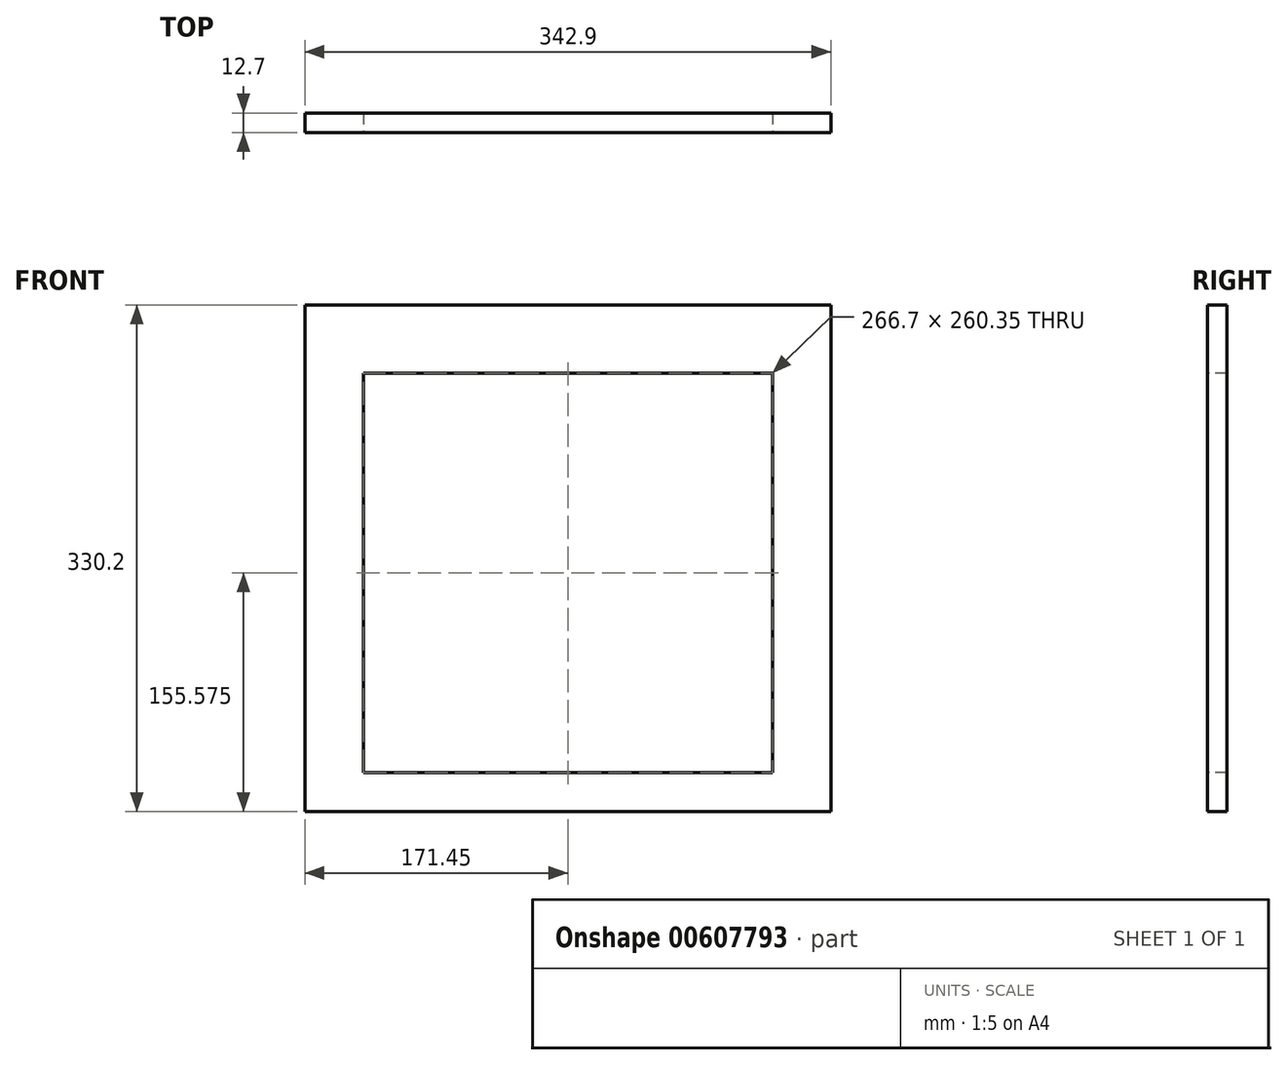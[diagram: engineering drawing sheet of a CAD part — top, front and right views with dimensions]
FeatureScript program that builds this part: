
annotation { "Feature Type Name" : "Feature", "Feature Type Description" : "" }
export const myFeature = defineFeature(function(context is Context, id is Id, definition is map)
    precondition{}
    {
        {
            var Q0;
            Q0=qCreatedBy(makeId("Front.planeOp"),FACE);
            var sketch = newSketch(context, id + "F0", { "sketchPlane" : qUnion([Q0])});
            skLineSegment(sketch, "E0.bottom", {"start": v(0, 0) * mm, "end": v(342.9, 0) * mm});
            skLineSegment(sketch, "E0.top", {"start": v(0, 330.2) * mm, "end": v(342.9, 330.2) * mm});
            skLineSegment(sketch, "E0.left", {"start": v(0, 0) * mm, "end": v(0, 330.2) * mm});
            skLineSegment(sketch, "E0.right", {"start": v(342.9, 0) * mm, "end": v(342.9, 330.2) * mm});
            skSolve(sketch);
        }
        {
            var Q0;
            Q0=makeQuery(id+"F0.imprint","IMPRINT",FACE,{"disambiguationData":[TD([[makeQuery(id+"F0.imprint","IMPRINT",EDGE,{"derivedFrom":sQuery(id+"F0.wireOp",EDGE,"E0.bottom")}),1.0]])]});
            extrude(context, id + "F1", {"entities" : qUnion([Q0]), "depth" : 12.7 * mm, "offsetDistance" : 25.4 * mm});
        }
        {
            var Q0;
            Q0=makeQuery(id+"F1.opExtrude","CAP_FACE",FACE,{"disambiguationData":[OSD([sQuery(id+"F0.wireOp",EDGE,"E0.bottom"),sQuery(id+"F0.wireOp",EDGE,"E0.top"),sQuery(id+"F0.wireOp",EDGE,"E0.left"),sQuery(id+"F0.wireOp",EDGE,"E0.right")])],"isStart":false});
            var sketch = newSketch(context, id + "F2", { "sketchPlane" : qUnion([Q0])});
            skLineSegment(sketch, "E1", {"start": v(0, 0) * mm, "end": v(0, 25.4) * mm});
            skLineSegment(sketch, "E2", {"start": v(0, 25.4) * mm, "end": v(38.1, 25.4) * mm});
            skLineSegment(sketch, "E3.bottom", {"start": v(38.1, 25.4) * mm, "end": v(304.8, 25.4) * mm});
            skLineSegment(sketch, "E3.top", {"start": v(38.1, 285.75) * mm, "end": v(304.8, 285.75) * mm});
            skLineSegment(sketch, "E3.left", {"start": v(38.1, 25.4) * mm, "end": v(38.1, 285.75) * mm});
            skLineSegment(sketch, "E3.right", {"start": v(304.8, 25.4) * mm, "end": v(304.8, 285.75) * mm});
            skSolve(sketch);
        }
        {
            var Q0;
            Q0=makeQuery(id+"F2.imprint","IMPRINT",FACE,{"disambiguationData":[TD([[makeQuery(id+"F2.imprint","IMPRINT",EDGE,{"derivedFrom":sQuery(id+"F2.wireOp",EDGE,"E3.bottom")}),1.0]])]});
            extrude(context, id + "F3", {"entities" : qUnion([Q0]), "operationType" : NewBodyOperationType.REMOVE, "oppositeDirection" : true, "depth" : 12.7 * mm, "offsetDistance" : 25.4 * mm});
        }
    });
